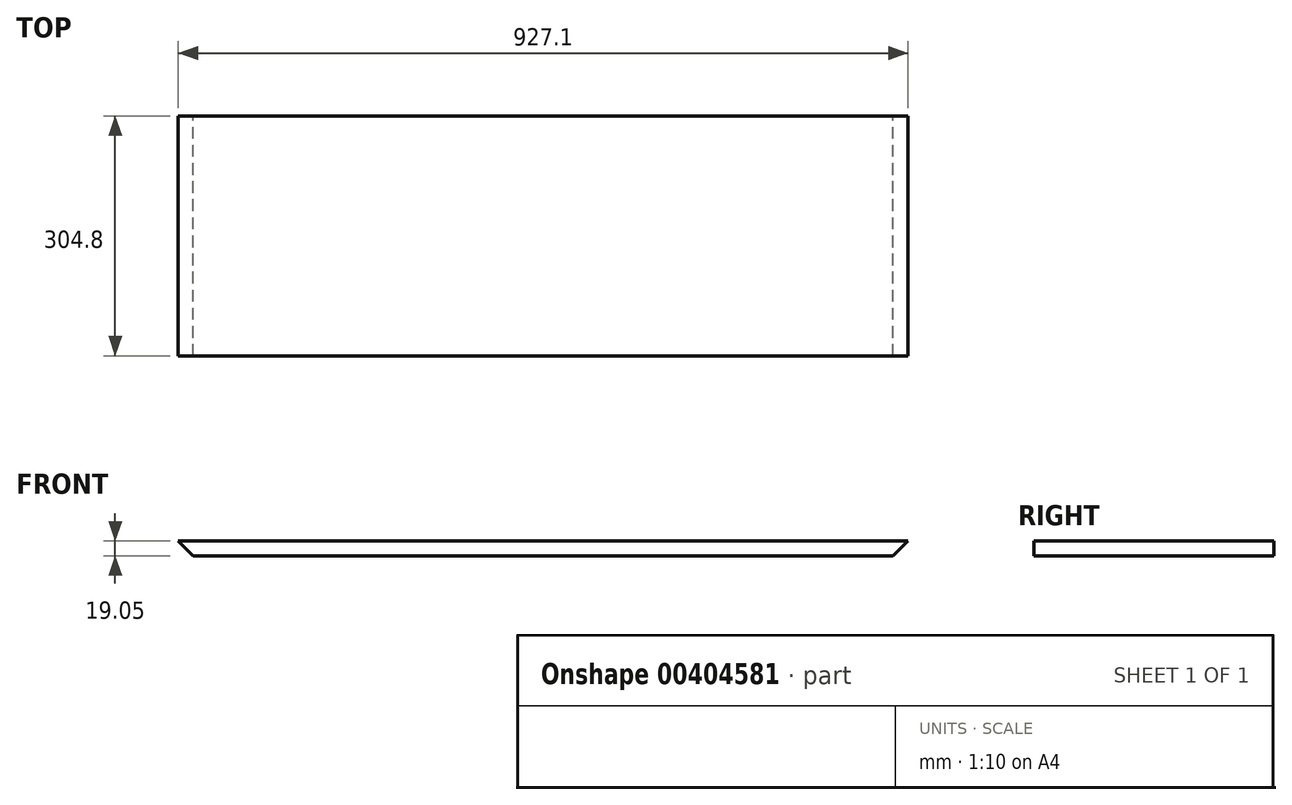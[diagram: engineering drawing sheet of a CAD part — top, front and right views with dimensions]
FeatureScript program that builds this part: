
annotation { "Feature Type Name" : "Feature", "Feature Type Description" : "" }
export const myFeature = defineFeature(function(context is Context, id is Id, definition is map)
    precondition{}
    {
        {
            var Q0;
            Q0=qCreatedBy(makeId("Front.planeOp"),FACE);
            var sketch = newSketch(context, id + "F0", { "sketchPlane" : qUnion([Q0])});
            skLineSegment(sketch, "E0.top", {"start": v(-444.5, 19.05) * mm, "end": v(444.5, 19.05) * mm});
            skLineSegment(sketch, "E1.MirrorCS", {"start": v(-463.55, 38.1) * mm, "end": v(463.55, 38.1) * mm});
            skLineSegment(sketch, "E2.MirrorCS", {"start": v(-463.55, 38.1) * mm, "end": v(-444.5, 19.05) * mm});
            skLineSegment(sketch, "E3.MirrorCS", {"start": v(463.55, 38.1) * mm, "end": v(444.5, 19.05) * mm});
            skSolve(sketch);
        }
        {
            var Q0;
            Q0 = qSketchRegion(id + "F0", true);
            extrude(context, id + "F1", {"entities" : qUnion([Q0]), "endBound" : BoundingType.SYMMETRIC, "depth" : 304.8 * mm});
        }
    });
